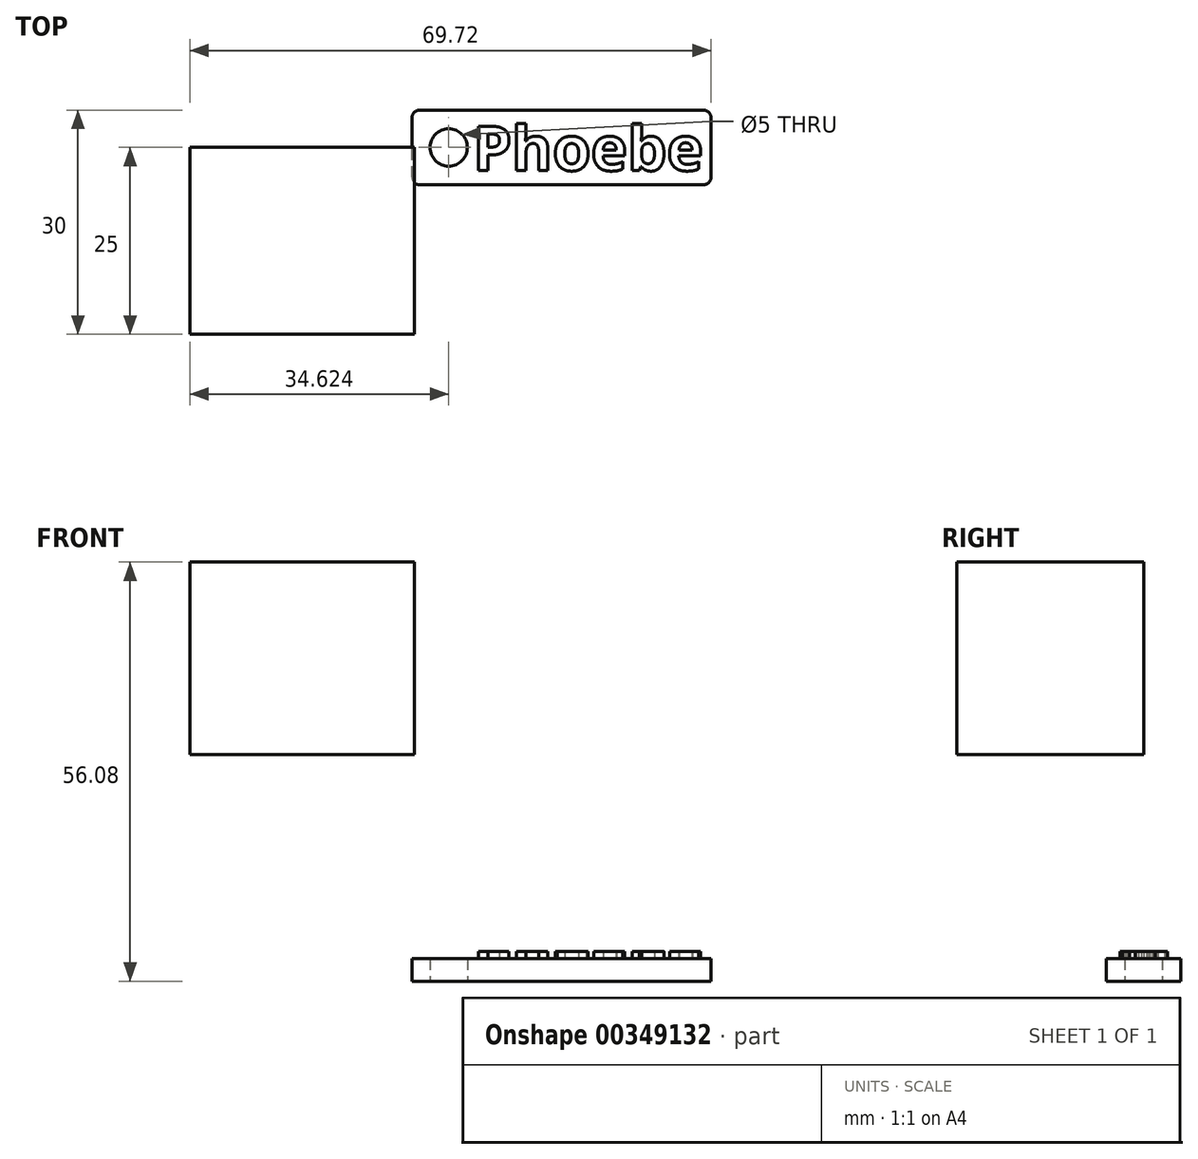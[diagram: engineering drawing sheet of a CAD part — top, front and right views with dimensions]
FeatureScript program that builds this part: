
annotation { "Feature Type Name" : "Feature", "Feature Type Description" : "" }
export const myFeature = defineFeature(function(context is Context, id is Id, definition is map)
    precondition{}
    {
        {
            var Q0;
            Q0=qCreatedBy(makeId("Top.planeOp"),FACE);
            var sketch = newSketch(context, id + "F0", { "sketchPlane" : qUnion([Q0])});
            skLineSegment(sketch, "E0.bottom", {"start": v(20, -5) * mm, "end": v(-20, -5) * mm});
            skLineSegment(sketch, "E0.top", {"start": v(20, 5) * mm, "end": v(-20, 5) * mm});
            skLineSegment(sketch, "E0.left", {"start": v(20, -5) * mm, "end": v(20, 5) * mm});
            skLineSegment(sketch, "E0.right", {"start": v(-20, -5) * mm, "end": v(-20, 5) * mm});
            skPoint(sketch, "E0.middle", {"position": v(0, 0) * mm});
            skCircle(sketch, "E1", {"center": v(-15.1, 0) * mm, "radius": 2.5 * mm});
            skSolve(sketch);
        }
        {
            var Q0;
            Q0=makeQuery(id+"F0.imprint","IMPRINT",FACE,{"disambiguationData":[TD([[makeQuery(id+"F0.imprint","IMPRINT",EDGE,{"derivedFrom":sQuery(id+"F0.wireOp",EDGE,"E0.bottom")}),-1.0]])]});
            extrude(context, id + "F1", {"entities" : qUnion([Q0]), "depth" : 3 * mm});
        }
        {
            var Q0;
            Q0=makeQuery(id+"F1.opExtrude","CAP_FACE",FACE,{"disambiguationData":[OSD([sQuery(id+"F0.wireOp",EDGE,"E0.bottom"),sQuery(id+"F0.wireOp",EDGE,"E0.top"),sQuery(id+"F0.wireOp",EDGE,"E0.left"),sQuery(id+"F0.wireOp",EDGE,"E0.right"),sQuery(id+"F0.wireOp",EDGE,"E1")])],"isStart":false});
            var sketch = newSketch(context, id + "F2", { "sketchPlane" : qUnion([Q0])});
            skText(sketch, "E2", { "text": "Phoebe", "fontName": "OpenSans-Bold.ttf"});
            const initialGuessF2  = {"E2": [-0.01186, -0.0031, 1, 0, 0.00597]};
            skSetInitialGuess(sketch, initialGuessF2);
            skSolve(sketch);
        }
        {
            var Q0;
            Q0 = qSketchRegion(id + "F2", true);
            extrude(context, id + "F3", {"entities" : qUnion([Q0]), "operationType" : NewBodyOperationType.ADD, "depth" : 1 * mm});
        }
        {
            var Q0;
            Q0=makeQuery(id+"F1.opExtrude","SWEPT_EDGE",EDGE,{"disambiguationData":[OSD([sQuery(id+"F0.wireOp",EDGE,"E0.bottom"),sQuery(id+"F0.wireOp",EDGE,"E0.right")])]});
            var Q1;
            Q1=makeQuery(id+"F1.opExtrude","SWEPT_EDGE",EDGE,{"disambiguationData":[OSD([sQuery(id+"F0.wireOp",EDGE,"E0.top"),sQuery(id+"F0.wireOp",EDGE,"E0.right")])]});
            var Q2;
            Q2=makeQuery(id+"F1.opExtrude","SWEPT_EDGE",EDGE,{"disambiguationData":[OSD([sQuery(id+"F0.wireOp",EDGE,"E0.bottom"),sQuery(id+"F0.wireOp",EDGE,"E0.left")])]});
            var Q3;
            Q3=makeQuery(id+"F1.opExtrude","SWEPT_EDGE",EDGE,{"disambiguationData":[OSD([sQuery(id+"F0.wireOp",EDGE,"E0.top"),sQuery(id+"F0.wireOp",EDGE,"E0.left")])]});
            fillet(context, id + "F4", {"entities" : qUnion([Q0, Q1, Q2, Q3]), "radius" : 1 * mm, "tangentPropagation" : true, "allowEdgeOverflow" : false});
        }
        {
            var Q0;
            Q0=qCreatedBy(makeId("Front.planeOp"),FACE);
            var sketch = newSketch(context, id + "F5", { "sketchPlane" : qUnion([Q0])});
            skLineSegment(sketch, "E3.bottom", {"start": v(-49.72, 56.08) * mm, "end": v(-19.66, 56.08) * mm});
            skLineSegment(sketch, "E3.top", {"start": v(-49.72, 30.35) * mm, "end": v(-19.66, 30.35) * mm});
            skLineSegment(sketch, "E3.left", {"start": v(-49.72, 56.08) * mm, "end": v(-49.72, 30.35) * mm});
            skLineSegment(sketch, "E3.right", {"start": v(-19.66, 56.08) * mm, "end": v(-19.66, 30.35) * mm});
            skSolve(sketch);
        }
        {
            var Q0;
            Q0=makeQuery(id+"F5.imprint","IMPRINT",FACE,{"disambiguationData":[TD([[makeQuery(id+"F5.imprint","IMPRINT",EDGE,{"derivedFrom":sQuery(id+"F5.wireOp",EDGE,"E3.bottom")}),-1.0]])]});
            extrude(context, id + "F6", {"entities" : qUnion([Q0]), "depth" : 25 * mm});
        }
    });
